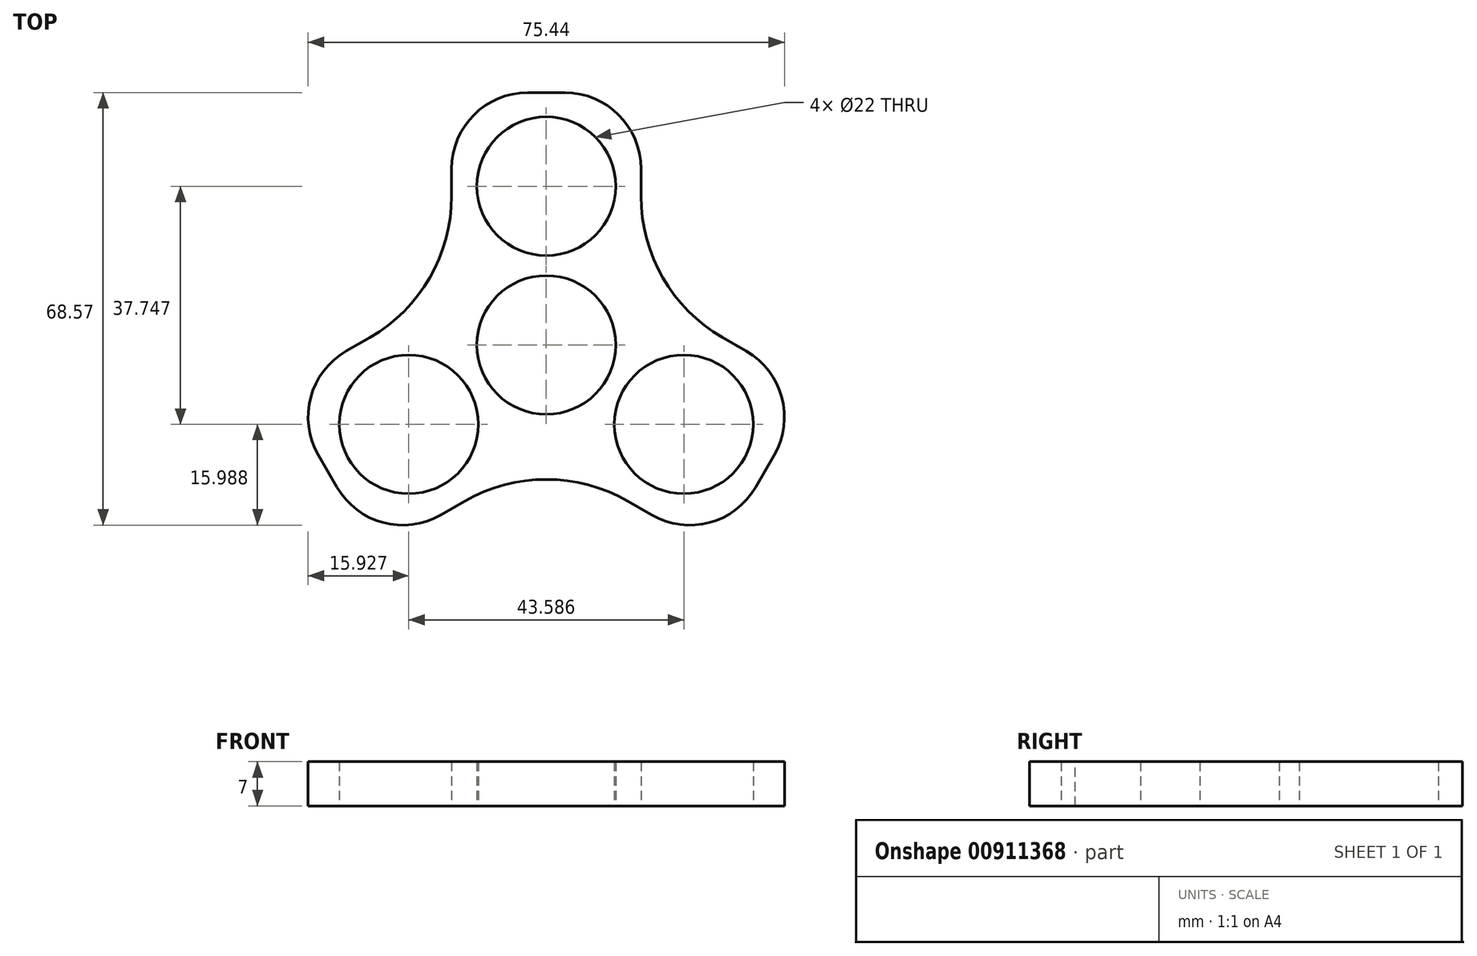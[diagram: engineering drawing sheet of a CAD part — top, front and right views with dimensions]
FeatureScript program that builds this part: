
annotation { "Feature Type Name" : "Feature", "Feature Type Description" : "" }
export const myFeature = defineFeature(function(context is Context, id is Id, definition is map)
    precondition{}
    {
        {
            var Q0;
            Q0=qCreatedBy(makeId("Top.planeOp"),FACE);
            var sketch = newSketch(context, id + "F0", { "sketchPlane" : qUnion([Q0])});
            skCircle(sketch, "E0", {"center": v(0, 0) * mm, "radius": 11 * mm});
            skLineSegment(sketch, "E1.bottom", {"start": v(0, 0) * mm, "end": v(15, 0) * mm});
            skLineSegment(sketch, "E1.top", {"start": v(0, 40) * mm, "end": v(15, 40) * mm});
            skLineSegment(sketch, "E1.left", {"start": v(0, 0) * mm, "end": v(0, 40) * mm});
            skLineSegment(sketch, "E1.right", {"start": v(15, 0) * mm, "end": v(15, 40) * mm});
            skLineSegment(sketch, "E2.bottom", {"start": v(0, 0) * mm, "end": v(-15, 0) * mm});
            skLineSegment(sketch, "E2.top", {"start": v(0, 40) * mm, "end": v(-15, 40) * mm});
            skLineSegment(sketch, "E2.right", {"start": v(-15, 0) * mm, "end": v(-15, 40) * mm});
            skLineSegment(sketch, "E3", {"start": v(0, 40) * mm, "end": v(0, 20) * mm});
            skLineSegment(sketch, "E4", {"start": v(0, 40) * mm, "end": v(0, 25.16) * mm});
            skCircle(sketch, "E5", {"center": v(0, 25.16) * mm, "radius": 11 * mm});
            skSolve(sketch);
        }
        {
            var Q0;
            {var subQ0=sQuery(id+"F0.wireOp",EDGE,"E2.top");Q0=makeQuery(id+"F0.imprint","IMPRINT",FACE,{"disambiguationData":[TD([[makeQuery(id+"F0.imprint","IMPRINT",EDGE,{"derivedFrom":subQ0}),1.0]])]});}
            var Q1;
            {var subQ5=sQuery(id+"F0.wireOp",EDGE,"E1.top");Q1=makeQuery(id+"F0.imprint","IMPRINT",FACE,{"disambiguationData":[TD([[makeQuery(id+"F0.imprint","IMPRINT",EDGE,{"derivedFrom":subQ5}),-1.0]])]});}
            extrude(context, id + "F1", {"entities" : qUnion([Q0, Q1]), "depth" : 7 * mm, "offsetDistance" : 25 * mm});
        }
        {
            var Q0;
            Q0=qCreatedBy(makeId("Front.planeOp"),FACE);
            var sketch = newSketch(context, id + "F2", { "sketchPlane" : qUnion([Q0])});
            skLineSegment(sketch, "E6", {"start": v(0, 0) * mm, "end": v(0, 44.53) * mm});
            skSolve(sketch);
        }
        {
            var Q0;
            Q0=makeQuery(id+"F1.opExtrude","SWEPT_BODY",BODY,{"disambiguationData":[OSD([sQuery(id+"F0.wireOp",EDGE,"E0"),sQuery(id+"F0.wireOp",EDGE,"E1.bottom"),sQuery(id+"F0.wireOp",EDGE,"E1.top"),sQuery(id+"F0.wireOp",EDGE,"E1.right"),sQuery(id+"F0.wireOp",EDGE,"E2.bottom"),sQuery(id+"F0.wireOp",EDGE,"E2.top"),sQuery(id+"F0.wireOp",EDGE,"E2.right"),sQuery(id+"F0.wireOp",EDGE,"E5")])]});
            var Q1;
            Q1=sQuery(id+"F2.wireOp",EDGE,"E6");
            transform(context, id + "F3", {"entities" : qUnion([Q0]), "transformType" : TransformType.ROTATION, "transformAxis" : qUnion([Q1]), "angle" : 120 * degree, "makeCopy" : true});
        }
        {
            var Q0;
            Q0=makeQuery(id+"F1.opExtrude","SWEPT_BODY",BODY,{"disambiguationData":[OSD([sQuery(id+"F0.wireOp",EDGE,"E0"),sQuery(id+"F0.wireOp",EDGE,"E1.bottom"),sQuery(id+"F0.wireOp",EDGE,"E1.top"),sQuery(id+"F0.wireOp",EDGE,"E1.right"),sQuery(id+"F0.wireOp",EDGE,"E2.bottom"),sQuery(id+"F0.wireOp",EDGE,"E2.top"),sQuery(id+"F0.wireOp",EDGE,"E2.right"),sQuery(id+"F0.wireOp",EDGE,"E5")])]});
            var Q1;
            Q1=sQuery(id+"F2.wireOp",EDGE,"E6");
            transform(context, id + "F4", {"entities" : qUnion([Q0]), "transformType" : TransformType.ROTATION, "transformAxis" : qUnion([Q1]), "angle" : 240 * degree, "makeCopy" : true});
        }
        {
            var Q0;
            Q0=makeQuery(id+"F1.opExtrude","SWEPT_BODY",BODY,{"disambiguationData":[OSD([sQuery(id+"F0.wireOp",EDGE,"E0"),sQuery(id+"F0.wireOp",EDGE,"E1.bottom"),sQuery(id+"F0.wireOp",EDGE,"E1.top"),sQuery(id+"F0.wireOp",EDGE,"E1.right"),sQuery(id+"F0.wireOp",EDGE,"E2.bottom"),sQuery(id+"F0.wireOp",EDGE,"E2.top"),sQuery(id+"F0.wireOp",EDGE,"E2.right"),sQuery(id+"F0.wireOp",EDGE,"E5")])]});
            var Q1;
            Q1=makeQuery(id+"F3.opPattern","COPY",BODY,{"derivedFrom":makeQuery(id+"F1.opExtrude","SWEPT_BODY",BODY,{"disambiguationData":[OSD([sQuery(id+"F0.wireOp",EDGE,"E0"),sQuery(id+"F0.wireOp",EDGE,"E1.bottom"),sQuery(id+"F0.wireOp",EDGE,"E1.top"),sQuery(id+"F0.wireOp",EDGE,"E1.right"),sQuery(id+"F0.wireOp",EDGE,"E2.bottom"),sQuery(id+"F0.wireOp",EDGE,"E2.top"),sQuery(id+"F0.wireOp",EDGE,"E2.right"),sQuery(id+"F0.wireOp",EDGE,"E5")])]}),"instanceName":"1"});
            var Q2;
            Q2=makeQuery(id+"F4.opPattern","COPY",BODY,{"derivedFrom":makeQuery(id+"F1.opExtrude","SWEPT_BODY",BODY,{"disambiguationData":[OSD([sQuery(id+"F0.wireOp",EDGE,"E0"),sQuery(id+"F0.wireOp",EDGE,"E1.bottom"),sQuery(id+"F0.wireOp",EDGE,"E1.top"),sQuery(id+"F0.wireOp",EDGE,"E1.right"),sQuery(id+"F0.wireOp",EDGE,"E2.bottom"),sQuery(id+"F0.wireOp",EDGE,"E2.top"),sQuery(id+"F0.wireOp",EDGE,"E2.right"),sQuery(id+"F0.wireOp",EDGE,"E5")])]}),"instanceName":"1"});
            booleanBodies(context, id + "F5", {"operationType" : BooleanOperationType.UNION, "tools" : qUnion([Q0, Q1, Q2])});
        }
        {
            var Q0;
            Q0=makeQuery(id+"F5.opBoolean","INTERSECT",EDGE,{"derivedFrom":[makeQuery(id+"F3.opPattern","COPY",FACE,{"derivedFrom":makeQuery(id+"F1.opExtrude","SWEPT_FACE",FACE,{"disambiguationData":[OSD([sQuery(id+"F0.wireOp",EDGE,"E2.right")])]}),"instanceName":"1"}),makeQuery(id+"F4.opPattern","COPY",FACE,{"derivedFrom":makeQuery(id+"F1.opExtrude","SWEPT_FACE",FACE,{"disambiguationData":[OSD([sQuery(id+"F0.wireOp",EDGE,"E1.right")])]}),"instanceName":"1"})]});
            fillet(context, id + "F6", {"entities" : qUnion([Q0]), "radius" : 25.86 * mm, "tangentPropagation" : true, "allowEdgeOverflow" : false});
        }
        {
            var Q0;
            Q0=makeQuery(id+"F5.opBoolean","INTERSECT",EDGE,{"derivedFrom":[makeQuery(id+"F1.opExtrude","SWEPT_FACE",FACE,{"disambiguationData":[OSD([sQuery(id+"F0.wireOp",EDGE,"E2.right")])]}),makeQuery(id+"F3.opPattern","COPY",FACE,{"derivedFrom":makeQuery(id+"F1.opExtrude","SWEPT_FACE",FACE,{"disambiguationData":[OSD([sQuery(id+"F0.wireOp",EDGE,"E1.right")])]}),"instanceName":"1"})]});
            fillet(context, id + "F7", {"entities" : qUnion([Q0]), "radius" : 25.86 * mm, "tangentPropagation" : true, "allowEdgeOverflow" : false});
        }
        {
            var Q0;
            Q0=makeQuery(id+"F5.opBoolean","INTERSECT",EDGE,{"derivedFrom":[makeQuery(id+"F1.opExtrude","SWEPT_FACE",FACE,{"disambiguationData":[OSD([sQuery(id+"F0.wireOp",EDGE,"E1.right")])]}),makeQuery(id+"F4.opPattern","COPY",FACE,{"derivedFrom":makeQuery(id+"F1.opExtrude","SWEPT_FACE",FACE,{"disambiguationData":[OSD([sQuery(id+"F0.wireOp",EDGE,"E2.right")])]}),"instanceName":"1"})]});
            fillet(context, id + "F8", {"entities" : qUnion([Q0]), "radius" : 25.86 * mm, "tangentPropagation" : true, "allowEdgeOverflow" : false});
        }
        {
            var Q0;
            Q0=makeQuery(id+"F3.opPattern","COPY",EDGE,{"derivedFrom":makeQuery(id+"F1.opExtrude","SWEPT_EDGE",EDGE,{"disambiguationData":[OSD([sQuery(id+"F0.wireOp",EDGE,"E2.top"),sQuery(id+"F0.wireOp",EDGE,"E2.right")])]}),"instanceName":"1"});
            fillet(context, id + "F9", {"entities" : qUnion([Q0]), "radius" : 12.07 * mm, "tangentPropagation" : true, "allowEdgeOverflow" : false});
        }
        {
            var Q0;
            Q0=makeQuery(id+"F3.opPattern","COPY",EDGE,{"derivedFrom":makeQuery(id+"F1.opExtrude","SWEPT_EDGE",EDGE,{"disambiguationData":[OSD([sQuery(id+"F0.wireOp",EDGE,"E1.top"),sQuery(id+"F0.wireOp",EDGE,"E1.right")])]}),"instanceName":"1"});
            fillet(context, id + "F10", {"entities" : qUnion([Q0]), "radius" : 12.07 * mm, "tangentPropagation" : true, "allowEdgeOverflow" : false});
        }
        {
            var Q0;
            Q0=makeQuery(id+"F1.opExtrude","SWEPT_EDGE",EDGE,{"disambiguationData":[OSD([sQuery(id+"F0.wireOp",EDGE,"E2.top"),sQuery(id+"F0.wireOp",EDGE,"E2.right")])]});
            fillet(context, id + "F11", {"entities" : qUnion([Q0]), "radius" : 12.07 * mm, "tangentPropagation" : true, "allowEdgeOverflow" : false});
        }
        {
            var Q0;
            Q0=makeQuery(id+"F1.opExtrude","SWEPT_EDGE",EDGE,{"disambiguationData":[OSD([sQuery(id+"F0.wireOp",EDGE,"E1.top"),sQuery(id+"F0.wireOp",EDGE,"E1.right")])]});
            fillet(context, id + "F12", {"entities" : qUnion([Q0]), "radius" : 12.07 * mm, "tangentPropagation" : true, "allowEdgeOverflow" : false});
        }
        {
            var Q0;
            Q0=makeQuery(id+"F4.opPattern","COPY",EDGE,{"derivedFrom":makeQuery(id+"F1.opExtrude","SWEPT_EDGE",EDGE,{"disambiguationData":[OSD([sQuery(id+"F0.wireOp",EDGE,"E1.top"),sQuery(id+"F0.wireOp",EDGE,"E1.right")])]}),"instanceName":"1"});
            fillet(context, id + "F13", {"entities" : qUnion([Q0]), "radius" : 12.07 * mm, "tangentPropagation" : true, "allowEdgeOverflow" : false});
        }
        {
            var Q0;
            Q0=makeQuery(id+"F4.opPattern","COPY",EDGE,{"derivedFrom":makeQuery(id+"F1.opExtrude","SWEPT_EDGE",EDGE,{"disambiguationData":[OSD([sQuery(id+"F0.wireOp",EDGE,"E2.top"),sQuery(id+"F0.wireOp",EDGE,"E2.right")])]}),"instanceName":"1"});
            fillet(context, id + "F14", {"entities" : qUnion([Q0]), "radius" : 12.07 * mm, "tangentPropagation" : true, "allowEdgeOverflow" : false});
        }
    });
